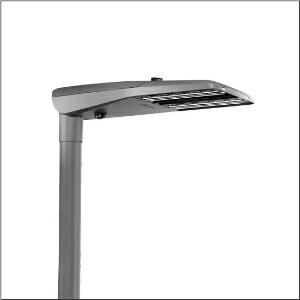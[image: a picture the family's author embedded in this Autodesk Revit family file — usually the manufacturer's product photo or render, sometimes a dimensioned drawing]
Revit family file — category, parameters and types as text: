
# Revit family: streetlight_sl_11_iq_midi___st1_0st0_5_5xc3j51y08me_1f9d
name_source: partatom
category: Lighting Fixtures
units: mm (PartAtom-declared; Revit-internal decimal feet)

## family parameters
Cut with Voids When Loaded = No
Host = Face
Light Source = No
Part Type = Normal
Room Calculation Point = No
Round Connector Dimension = Use Diameter
Shared = No

## types (1)
- --- (1 x LED, 17650 lm, 122.7 W, 3000K)
    Apparent Load = 123 VA
    CIE Flux Codes = 35 68 96 100 100
    Color Rendering = 70
    Color Temperature = 3000K
    Default Elevation = 1800 mm
    Description = Streetlight SL 11 iQ midi, mast luminaire, primary light control with 3 zone facetted reflector, of plastic, silver coated, highly specular, primary optical cover: cover, of PMMA, transparent, light distribution: ST1.0ST0.5, light emission: direct distribution, primary light characteristic: asymmetric, installation type: post-top, side-entry, LED, High Power LED, rated luminous flux: 17.650lm, luminous efficacy: 144lm/W, light colour: 730, colour temperature: 3000K, control: pre-setting: logarithmic dimming characteristic, Street-Remote, Auto-Match, Temp-Guard, Lumen-Switch, Night-Set, Smart-Wire, Light-Fading, Desk-Remote (wireless, voltage-free reading and setting of iQ features in the workshop via application-optimized NFC function/RFID function), optimised constant luminous flux control (CLO 2.0), with cable H07RN-F 5x 1.5mm², mains connection: 230..240V, AC, 50/60Hz, connection cable pre-assembled, cable length: 12,5m, start of lifetime: 123W, end of service life: 130W, reduction: 56W, luminaire housing, of diecast aluminium, powder-coated, Siteco® metallic grey (DB 702S), please order mast flange separately, inclination adjustable without tools: 0°, 5°, 10°, 15° (post-top) | 0°, -5°, -10°, -15° (side-entry), sealing non-destructively replaceable, multi-level sealing system, length: 780mm, width: 376mm, height: 118mm, mast flange for spigot size: 42mm (side-entry): 5XC10008XM4, 60/48mm (side-entry/post-top): 5XC10108XM2, 76/60mm (side-entry/post-top): 5XC10108XM1, equipment: Power, Smart Interface below and above, protection rating (complete): IP66, insulation class (complete): insulation class II (safety insulation), certification: CE, ENEC, VDE, UKCA, impact resistance: IK09, permissible operating ambient temperature for outdoor applications: -25..+50°C, standard-compliant lighting for roads and squares, Environmental Product Declaration (EPD) tested and certified by an independent institute, packaging unit: 1 piece

Light Distribution: ST1.0ST0.5
    Height = 118 mm
    Lamp = 1 x LED
    Lamp Light Flux = 17650 lm
    Lamp Power = 122.7 W
    Lamp count = 1
    Length = 780 mm
    Luminous efficacy = 144 lm/W
    Manufacturer = Siteco
    ModVariant = No
    Model = 5XC3J51Y08ME
    Number of Poles = 1
    OnlyDefault = Yes
    Power Factor = 1
    Product Name = Streetlight SL 11 iQ midi | ST1.0ST0.5
    Product group = mast luminaire | pylon top
    ProductGroupID = 6100
    Protection Class = Protection class II
    Protection Degree = IP 66
    RLX_Detail_Level = 1
    RLX_Emergency_Light_Flux = 0 lm
    RLX_Emergency_Type = 0
    RLX_Emergency_Type_DB = No
    RlxData = <blob elided: 69585 chars, md5=df93d322>
    Socket = socket
    Standby Power = 0 W
    System Light Flux = 17650 lm
    System Power = 123 W
    Type Comments = factory setting: luminous flux: 100 % | dim-lin: 254 | 553 mA
    Type Image = l_1004429.jpg
    URL = http://relux.com
    VarID = @adj_008773
    Voltage = 0 V
    Weight = 0.00 kg
    Width = 376 mm

## geometry (parser evidence)
native form markers: Blend x4, Sweep x8
no freeform markers — native parametric forms only
